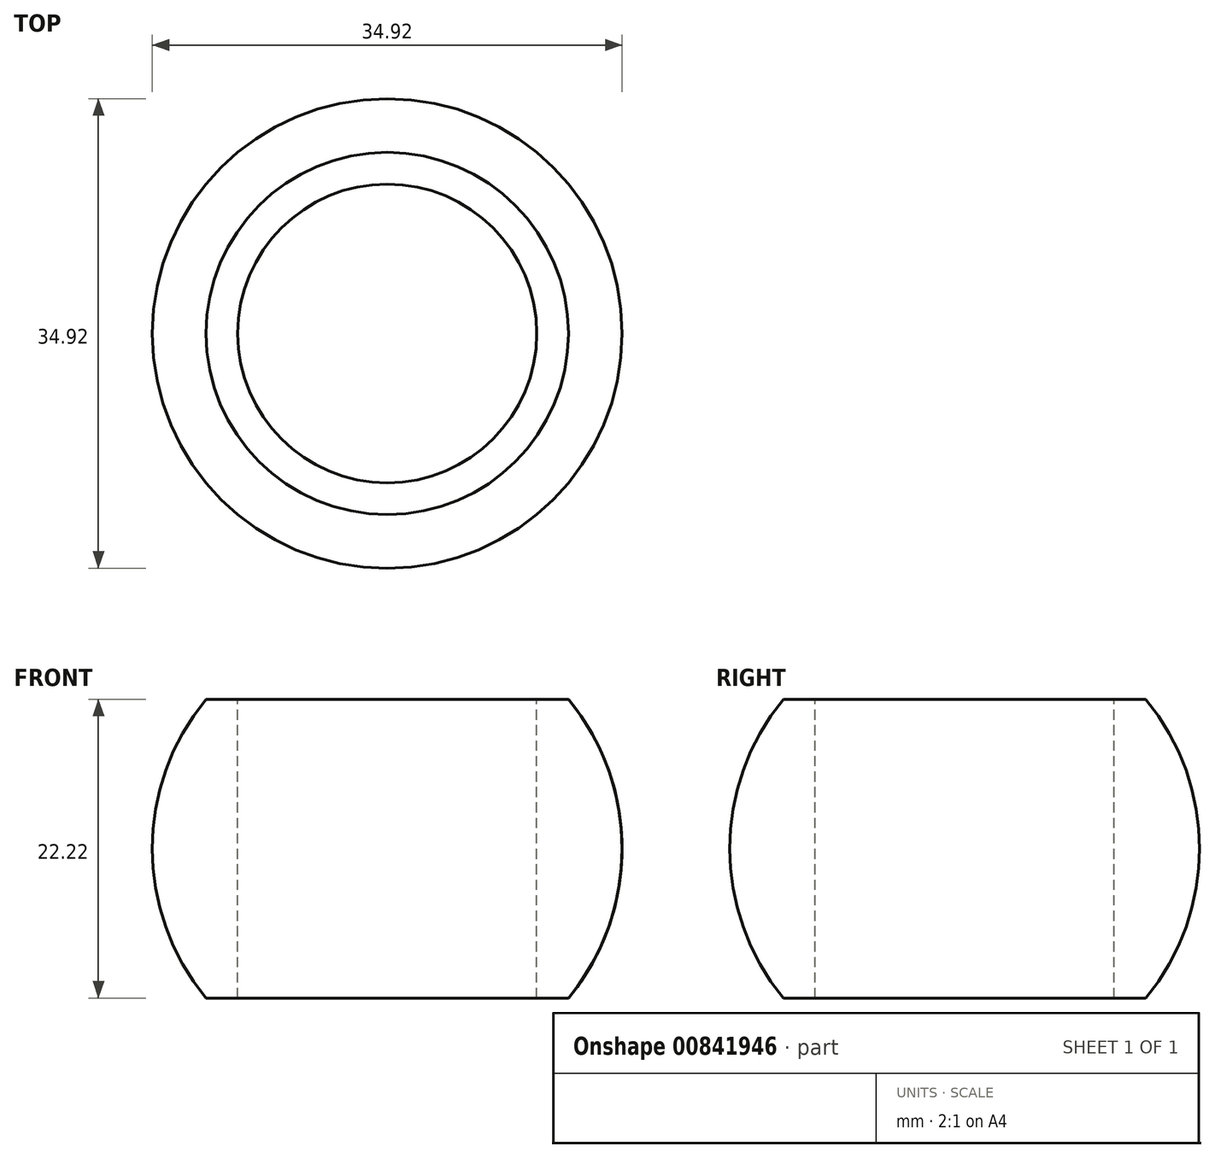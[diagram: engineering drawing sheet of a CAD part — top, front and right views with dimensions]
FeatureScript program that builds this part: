
annotation { "Feature Type Name" : "Feature", "Feature Type Description" : "" }
export const myFeature = defineFeature(function(context is Context, id is Id, definition is map)
    precondition{}
    {
        {
            var Q0;
            Q0=qCreatedBy(makeId("Front.planeOp"),FACE);
            var sketch = newSketch(context, id + "F0", { "sketchPlane" : qUnion([Q0])});
            skArc(sketch, "E0", {"start": v(-13.47, 11.11) * mm, "mid": v(-17.46, 0) * mm, "end": v(-13.47, -11.11) * mm});
            skLineSegment(sketch, "E1", {"start": v(0, 11.11) * mm, "end": v(0, -11.11) * mm, "construction": true});
            skLineSegment(sketch, "E2", {"start": v(-13.47, 11.11) * mm, "end": v(-11.11, 11.11) * mm});
            skLineSegment(sketch, "E3", {"start": v(-11.11, -11.11) * mm, "end": v(-13.47, -11.11) * mm});
            skPoint(sketch, "E4.orphan", {"position": v(0, 17.46) * mm});
            skLineSegment(sketch, "E5", {"start": v(-11.11, 11.11) * mm, "end": v(-11.11, -11.11) * mm});
            skSolve(sketch);
        }
        {
            var Q0;
            Q0=qSketchRegion(id+"F0",true);
            var Q1;
            Q1=sQuery(id+"F0.wireOp",EDGE,"E1");
            revolve(context, id + "F1", {"surfaceOperationType" : NewSurfaceOperationType.NEW, "entities" : qUnion([Q0]), "axis" : qUnion([Q1]), "revolveType" : RevolveType.FULL});
        }
    });
